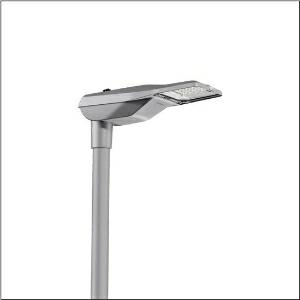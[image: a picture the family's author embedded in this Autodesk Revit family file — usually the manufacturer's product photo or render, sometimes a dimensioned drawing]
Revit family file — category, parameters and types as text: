
# Revit family: streetlight_sl_21_iq_micro___p0_8a_5xe1u31v08db_560e
name_source: partatom
category: Lighting Fixtures
units: mm (PartAtom-declared; Revit-internal decimal feet)

## family parameters
Cut with Voids When Loaded = No
Host = Face
Light Source = No
Part Type = Normal
Room Calculation Point = No
Round Connector Dimension = Use Diameter
Shared = No

## types (1)
- --- (1 x LED, 5130 lm, 39.1 W, 3000K)
    Apparent Load = 39 VA
    CIE Flux Codes = 33 69 96 100 100
    Color Rendering = 70
    Color Temperature = 3000K
    Default Elevation = 1800 mm
    Description = Streetlight SL 21 iQ micro, mast luminaire, primary light control with lens, of PMMA, primary optical cover: cover, of toughened safety glass, transparent, light distribution: P0.8a, light emission: direct distribution, primary light characteristic: asymmetric, installation type: post-top, side-entry, LED, High Power LED, rated luminous flux: 5.130lm, luminous efficacy: 131lm/W, light colour: 730, colour temperature: 3000K, control gear: iQ-Street Remote, D4i with power reduction, control: pre-setting: logarithmic dimming characteristic, Street-Remote, Auto-Match, Temp-Guard, Lumen-Switch, Night-Set, Smart-Wire, Light-Fading, Desk-Remote (wireless, voltage-free reading and setting of iQ features in the workshop via application-optimized NFC function/RFID function), optimised constant luminous flux control (CLO 2.0), mains connection: 220..240V, AC, 50/60Hz, start of lifetime: 39W, end of service life: 41W, reduction: 17W, luminaire housing, of diecast aluminium, powder-coated, SITECO metallic grey (DB 702S), corrosivity category C5 high according to DIN EN ISO 12944, please order mast flange separately, inclination adjustable: 0°, 5°, 10°, 15°, sealing non-destructively replaceable, multi-level sealing system, length: 528mm, width: 235mm, height: 110mm, mast flange for spigot size: 42mm (side-entry): 5XC10008XM4, 60/48mm (side-entry/post-top): 5XC10108XM2, 76/60mm (side-entry/post-top): 5XC10108XM1, mounting height: 4..8m, Smart Interface above, protection rating (complete): IP66, insulation class (complete): insulation class II (safety insulation), certification: CE, ENEC, ENEC+, VDE, impact resistance: IK10, permissible operating ambient temperature for outdoor applications: -40..+50°C, standard-compliant lighting for roads and squares, packaging unit: 1 piece

Light Distribution: P0.8a
    Height = 110 mm
    Lamp = 1 x LED
    Lamp Light Flux = 5130 lm
    Lamp Power = 39.1 W
    Lamp count = 1
    Length = 528 mm
    Luminous efficacy = 131 lm/W
    Manufacturer = Siteco
    ModVariant = No
    Model = 5XE1U31V08DB
    Number of Poles = 1
    OnlyDefault = Yes
    Power Factor = 1
    Product Name = Streetlight SL 21 iQ micro | P0.8a
    Product group = mast luminaire | pylon top
    ProductGroupID = 6100
    Protection Class = Protection class II
    Protection Degree = IP 66
    RLX_Detail_Level = 1
    RLX_Emergency_Light_Flux = 0 lm
    RLX_Emergency_Type = 0
    RLX_Emergency_Type_DB = No
    RlxData = <blob elided: 98253 chars, md5=8ce0dbbd>
    Socket = socket
    Standby Power = 0 W
    System Light Flux = 5130 lm
    System Power = 39 W
    Type Comments = factory setting: luminous flux: 100 % | dim-lin: 254 | 765 mA
    Type Image = l_1277292.jpg
    URL = http://relux.com
    VarID = @adj_082035
    Voltage = 0 V
    Weight = 0.00 kg
    Width = 235 mm

## geometry (parser evidence)
native form markers: Blend x4, Sweep x12
no freeform markers — native parametric forms only
